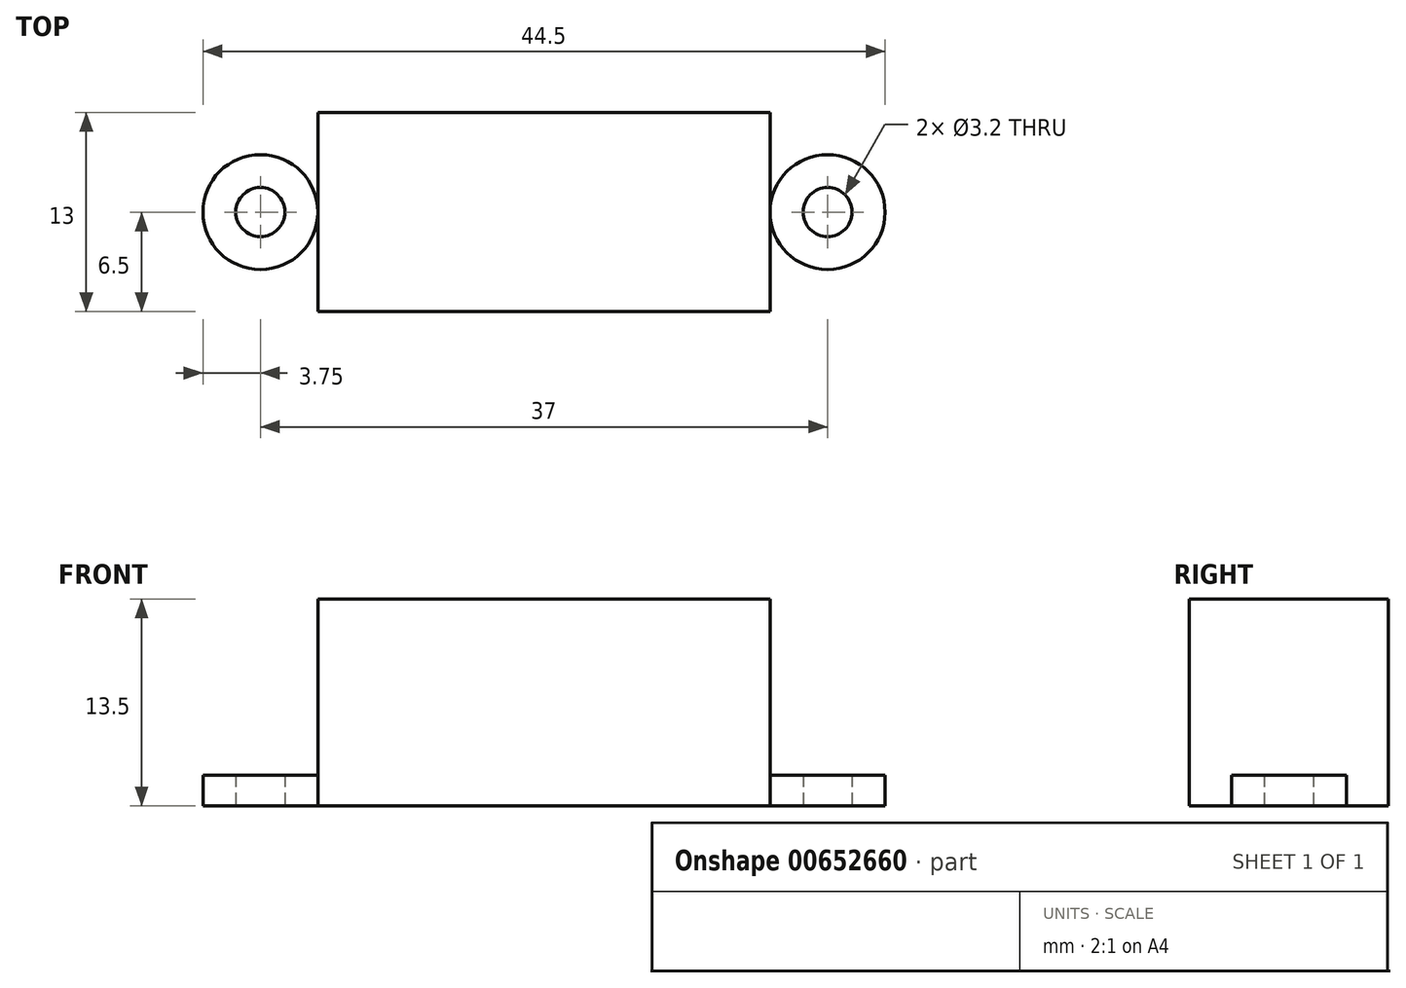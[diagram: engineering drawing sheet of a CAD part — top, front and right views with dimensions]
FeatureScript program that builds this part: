
annotation { "Feature Type Name" : "Feature", "Feature Type Description" : "" }
export const myFeature = defineFeature(function(context is Context, id is Id, definition is map)
    precondition{}
    {
        {
            var Q0;
            Q0=qCreatedBy(makeId("Top.planeOp"),FACE);
            var sketch = newSketch(context, id + "F0", { "sketchPlane" : qUnion([Q0])});
            skLineSegment(sketch, "E0.bottom", {"start": v(-14.75, -6.5) * mm, "end": v(14.75, -6.5) * mm});
            skLineSegment(sketch, "E0.top", {"start": v(-14.75, 6.5) * mm, "end": v(14.75, 6.5) * mm});
            skLineSegment(sketch, "E0.left", {"start": v(-14.75, -6.5) * mm, "end": v(-14.75, 6.5) * mm});
            skLineSegment(sketch, "E0.right", {"start": v(14.75, -6.5) * mm, "end": v(14.75, 6.5) * mm});
            skPoint(sketch, "E0.middle", {"position": v(0, 0) * mm});
            skSolve(sketch);
        }
        {
            var Q0;
            Q0=qCreatedBy(makeId("Top.planeOp"),FACE);
            var sketch = newSketch(context, id + "F1", { "sketchPlane" : qUnion([Q0])});
            skCircle(sketch, "E1", {"center": v(18.5, 0) * mm, "radius": 3.75 * mm});
            skCircle(sketch, "E2", {"center": v(-18.5, 0) * mm, "radius": 3.75 * mm});
            skCircle(sketch, "E3", {"center": v(18.5, 0) * mm, "radius": 1.6 * mm});
            skCircle(sketch, "E4", {"center": v(-18.5, 0) * mm, "radius": 1.6 * mm});
            skSolve(sketch);
        }
        {
            var Q0;
            Q0=makeQuery(id+"F0.imprint","IMPRINT",FACE,{"disambiguationData":[TD([[makeQuery(id+"F0.imprint","IMPRINT",EDGE,{"derivedFrom":sQuery(id+"F0.wireOp",EDGE,"E0.bottom")}),1.0]])]});
            extrude(context, id + "F2", {"entities" : qUnion([Q0]), "depth" : 13.5 * mm, "offsetDistance" : 25 * mm});
        }
        {
            var Q0;
            Q0=makeQuery(id+"F1.imprint","IMPRINT",FACE,{"disambiguationData":[TD([[makeQuery(id+"F1.imprint","IMPRINT",EDGE,{"derivedFrom":sQuery(id+"F1.wireOp",EDGE,"E2")}),1.0]])]});
            var Q1;
            Q1=makeQuery(id+"F1.imprint","IMPRINT",FACE,{"disambiguationData":[TD([[makeQuery(id+"F1.imprint","IMPRINT",EDGE,{"derivedFrom":sQuery(id+"F1.wireOp",EDGE,"E1")}),1.0]])]});
            var Q2;
            Q2=sQuery(id+"F1.wireOp",EDGE,"E2");
            var Q3;
            Q3=sQuery(id+"F1.wireOp",EDGE,"E1");
            extrude(context, id + "F3", {"entities" : qUnion([Q0, Q1]), "operationType" : NewBodyOperationType.ADD, "surfaceEntities" : qUnion([Q2, Q3]), "depth" : 2 * mm, "offsetDistance" : 25 * mm});
        }
    });
